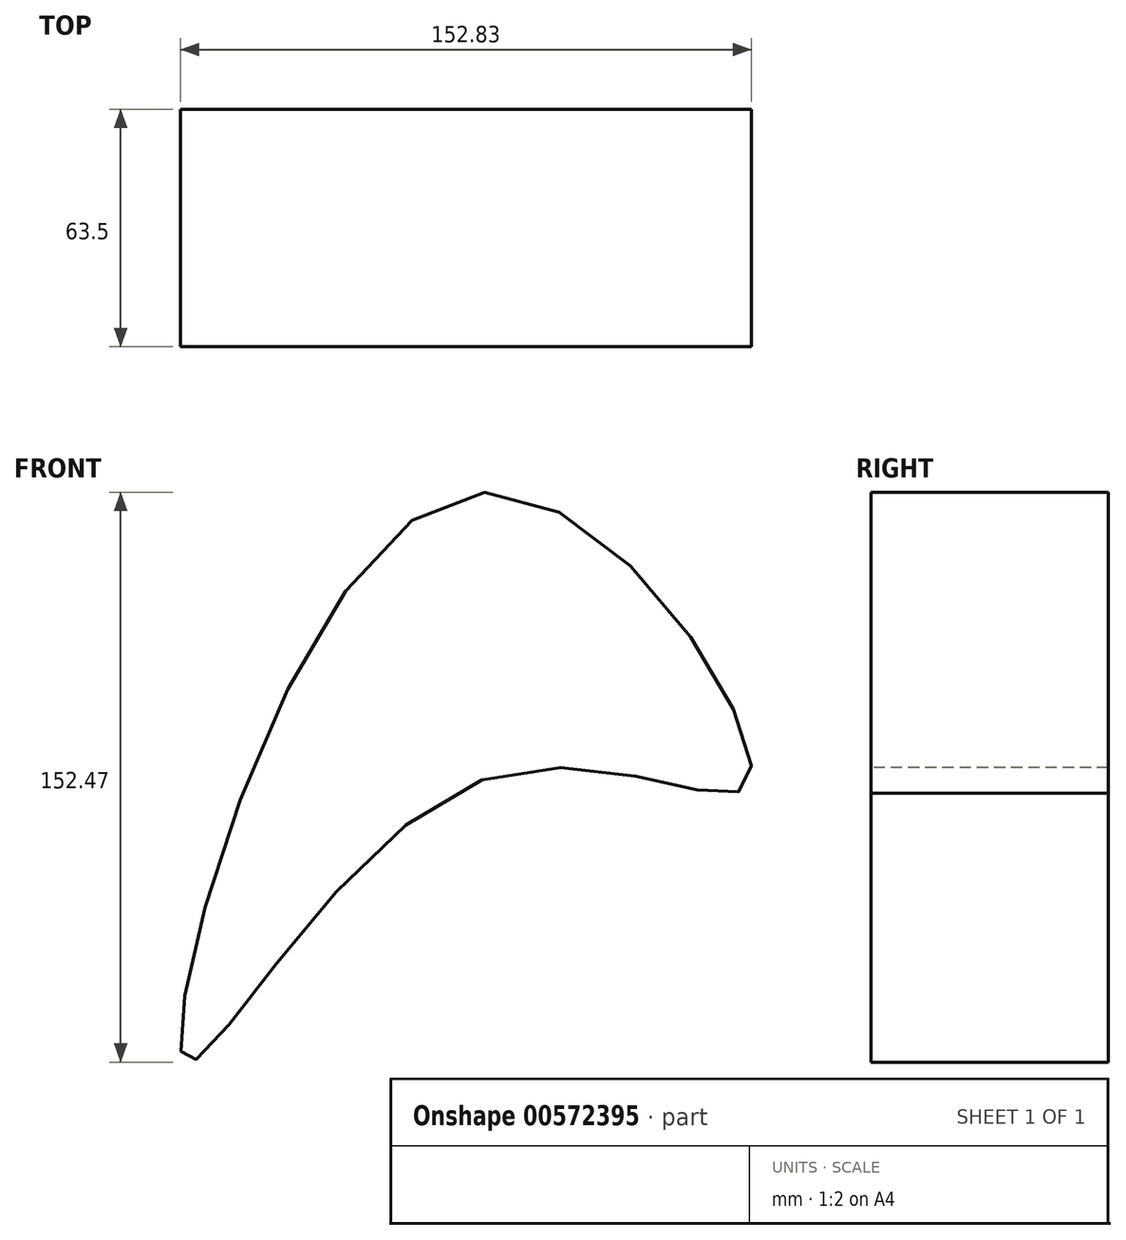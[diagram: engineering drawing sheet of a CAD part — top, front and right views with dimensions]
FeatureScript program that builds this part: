
annotation { "Feature Type Name" : "Feature", "Feature Type Description" : "" }
export const myFeature = defineFeature(function(context is Context, id is Id, definition is map)
    precondition{}
    {
        {
            var Q0;
            Q0=qCreatedBy(makeId("Front.planeOp"),FACE);
            var sketch = newSketch(context, id + "F0", { "sketchPlane" : qUnion([Q0])});
            skFitSpline(sketch, "E0", {"points": [v(4.3, 0) * mm, v(76.13, 0) * mm, v(0, 76.36) * mm, v(-75.42, -74.74) * mm, v(4.3, 0) * mm]});
            skSolve(sketch);
        }
        {
            var Q0;
            Q0=makeQuery(id+"F0.imprint","IMPRINT",FACE,{"disambiguationData":[TD([[makeQuery(id+"F0.imprint","IMPRINT",EDGE,{"derivedFrom":sQuery(id+"F0.wireOp",EDGE,"E0")}),1.0]])]});
            extrude(context, id + "F1", {"entities" : qUnion([Q0]), "depth" : 38.1 * mm, "offsetDistance" : 25.4 * mm});
        }
        {
            var Q0;
            Q0=makeQuery(id+"F1.opExtrude","CAP_FACE",FACE,{"disambiguationData":[OSD([sQuery(id+"F0.wireOp",EDGE,"E0")])],"isStart":false});
            var sketch = newSketch(context, id + "F2", { "sketchPlane" : qUnion([Q0])});
            skArc(sketch, "E1", {"start": v(0, 27.02) * mm, "mid": v(23.63, 11.99) * mm, "end": v(46.73, 27.82) * mm});
            skSolve(sketch);
        }
        {
            var Q0;
            Q0=sQuery(id+"F2.wireOp",EDGE,"E1");
            extrude(context, id + "F3", {"bodyType" : ToolBodyType.SURFACE, "surfaceEntities" : qUnion([Q0]), "depth" : 25.4 * mm, "offsetDistance" : 25.4 * mm});
        }
        {
            var Q0;
            Q0=makeQuery(id+"F1.opExtrude","CAP_FACE",FACE,{"disambiguationData":[OSD([sQuery(id+"F0.wireOp",EDGE,"E0")])],"isStart":false});
            var sketch = newSketch(context, id + "F4", { "sketchPlane" : qUnion([Q0])});
            skLineSegment(sketch, "E2", {"start": v(9.06, 62.35) * mm, "end": v(9.06, 48.01) * mm});
            skLineSegment(sketch, "E3", {"start": v(9.06, 48.01) * mm, "end": v(14.67, 48.01) * mm});
            skLineSegment(sketch, "E4", {"start": v(14.67, 48.01) * mm, "end": v(14.67, 62.04) * mm});
            skLineSegment(sketch, "E5", {"start": v(14.67, 62.04) * mm, "end": v(9.06, 62.35) * mm});
            skLineSegment(sketch, "E6", {"start": v(24.95, 62.04) * mm, "end": v(24.95, 48.01) * mm});
            skLineSegment(sketch, "E7", {"start": v(24.95, 48.01) * mm, "end": v(31.5, 48.01) * mm});
            skLineSegment(sketch, "E8", {"start": v(31.5, 48.01) * mm, "end": v(31.5, 62.04) * mm});
            skLineSegment(sketch, "E9", {"start": v(31.5, 62.04) * mm, "end": v(24.95, 62.04) * mm});
            skLineSegment(sketch, "E10", {"start": v(14.67, 62.04) * mm, "end": v(17.16, 62.35) * mm});
            skLineSegment(sketch, "E11", {"start": v(17.16, 62.35) * mm, "end": v(17.16, 48.01) * mm});
            skSolve(sketch);
        }
        {
            var Q0;
            Q0=makeQuery(id+"F4.imprint","IMPRINT",FACE,{"disambiguationData":[TD([[makeQuery(id+"F4.imprint","IMPRINT",EDGE,{"derivedFrom":sQuery(id+"F4.wireOp",EDGE,"E2")}),1.0]])]});
            var Q1;
            Q1=makeQuery(id+"F4.imprint","IMPRINT",FACE,{"disambiguationData":[TD([[makeQuery(id+"F4.imprint","IMPRINT",EDGE,{"derivedFrom":sQuery(id+"F4.wireOp",EDGE,"E6")}),1.0]])]});
            var Q2;
            Q2=makeQuery(id+"F4.imprint","IMPRINT",FACE,{"disambiguationData":[TD([[makeQuery(id+"F4.imprint","IMPRINT",EDGE,{"derivedFrom":sQuery(id+"F4.wireOp",EDGE,"E2")}),-1.0]])]});
            extrude(context, id + "F5", {"entities" : qUnion([Q0, Q1, Q2]), "operationType" : NewBodyOperationType.ADD, "depth" : 25.4 * mm, "offsetDistance" : 25.4 * mm});
        }
    });
